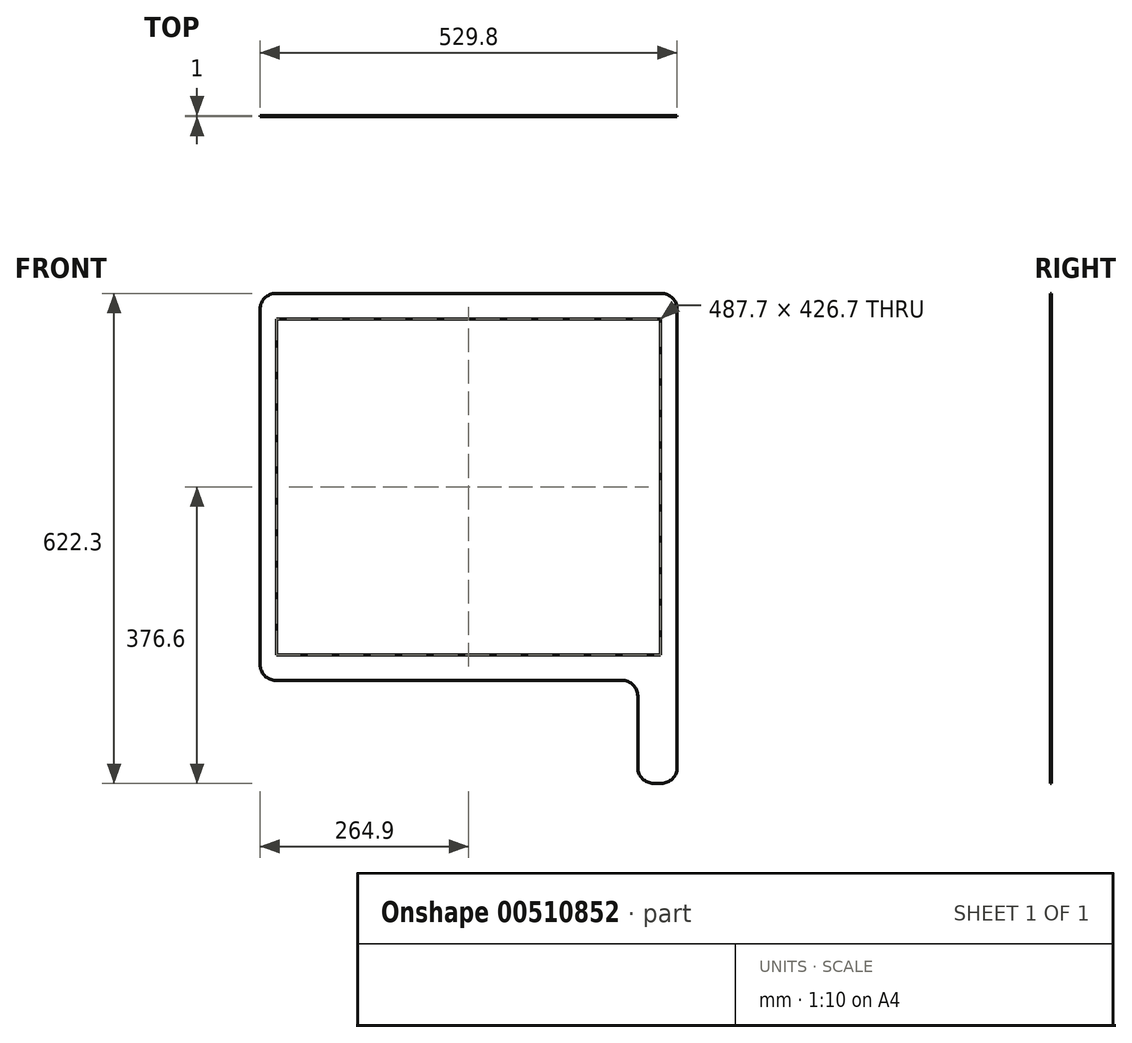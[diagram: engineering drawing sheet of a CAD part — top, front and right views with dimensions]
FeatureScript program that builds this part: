
annotation { "Feature Type Name" : "Feature", "Feature Type Description" : "" }
export const myFeature = defineFeature(function(context is Context, id is Id, definition is map)
    precondition{}
    {
        {
            var Q0;
            Q0=qCreatedBy(makeId("Front.planeOp"),FACE);
            var sketch = newSketch(context, id + "F0", { "sketchPlane" : qUnion([Q0])});
            skLineSegment(sketch, "E0.bottom", {"start": v(20, 0) * mm, "end": v(459.8, 0) * mm});
            skLineSegment(sketch, "E0.top", {"start": v(20, 491.4) * mm, "end": v(509.8, 491.4) * mm});
            skLineSegment(sketch, "E0.left", {"start": v(0, 20) * mm, "end": v(0, 471.4) * mm});
            skLineSegment(sketch, "E0.right", {"start": v(529.8, 0) * mm, "end": v(529.8, 471.4) * mm});
            skLineSegment(sketch, "E1.top", {"start": v(509.8, -130.9) * mm, "end": v(499.8, -130.9) * mm});
            skLineSegment(sketch, "E1.left", {"start": v(529.8, 0) * mm, "end": v(529.8, -110.9) * mm});
            skLineSegment(sketch, "E1.right", {"start": v(479.8, -20) * mm, "end": v(479.8, -110.9) * mm});
            skLineSegment(sketch, "E2.bottom", {"start": v(21.05, 459.05) * mm, "end": v(508.75, 459.05) * mm});
            skLineSegment(sketch, "E2.top", {"start": v(21.05, 32.35) * mm, "end": v(508.75, 32.35) * mm});
            skLineSegment(sketch, "E2.left", {"start": v(21.05, 459.05) * mm, "end": v(21.05, 32.35) * mm});
            skLineSegment(sketch, "E2.right", {"start": v(508.75, 459.05) * mm, "end": v(508.75, 32.35) * mm});
            skLineSegment(sketch, "E3", {"start": v(264.9, 491.4) * mm, "end": v(264.9, -45.28) * mm, "construction": true});
            skPoint(sketch, "E4.endSnap0", {"position": v(0, 245.7) * mm});
            skLineSegment(sketch, "E5", {"start": v(695.09, 245.7) * mm, "end": v(0, 245.7) * mm, "construction": true});
            skPoint(sketch, "E6.visualSharp", {"position": v(0, 491.4) * mm});
            skArc(sketch, "E6.filletArc", {"start": v(20, 491.4) * mm, "mid": v(5.86, 485.54) * mm, "end": v(0, 471.4) * mm});
            skPoint(sketch, "E7.visualSharp", {"position": v(0, 0) * mm});
            skArc(sketch, "E7.filletArc", {"start": v(0, 20) * mm, "mid": v(5.86, 5.86) * mm, "end": v(20, 0) * mm});
            skPoint(sketch, "E8.visualSharp", {"position": v(479.8, 0) * mm});
            skArc(sketch, "E8.filletArc", {"start": v(479.8, -20) * mm, "mid": v(473.94, -5.86) * mm, "end": v(459.8, 0) * mm});
            skPoint(sketch, "E9.visualSharp", {"position": v(529.8, 491.4) * mm});
            skArc(sketch, "E9.filletArc", {"start": v(529.8, 471.4) * mm, "mid": v(523.94, 485.54) * mm, "end": v(509.8, 491.4) * mm});
            skPoint(sketch, "E10.visualSharp", {"position": v(529.8, -130.9) * mm});
            skArc(sketch, "E10.filletArc", {"start": v(509.8, -130.9) * mm, "mid": v(523.94, -125.04) * mm, "end": v(529.8, -110.9) * mm});
            skPoint(sketch, "E11.visualSharp", {"position": v(479.8, -130.9) * mm});
            skArc(sketch, "E11.filletArc", {"start": v(479.8, -110.9) * mm, "mid": v(485.66, -125.04) * mm, "end": v(499.8, -130.9) * mm});
            skSolve(sketch);
        }
        {
            var Q0;
            Q0 = qSketchRegion(id + "F0", true);
            extrude(context, id + "F1", {"entities" : qUnion([Q0]), "depth" : 1 * mm});
        }
    });
